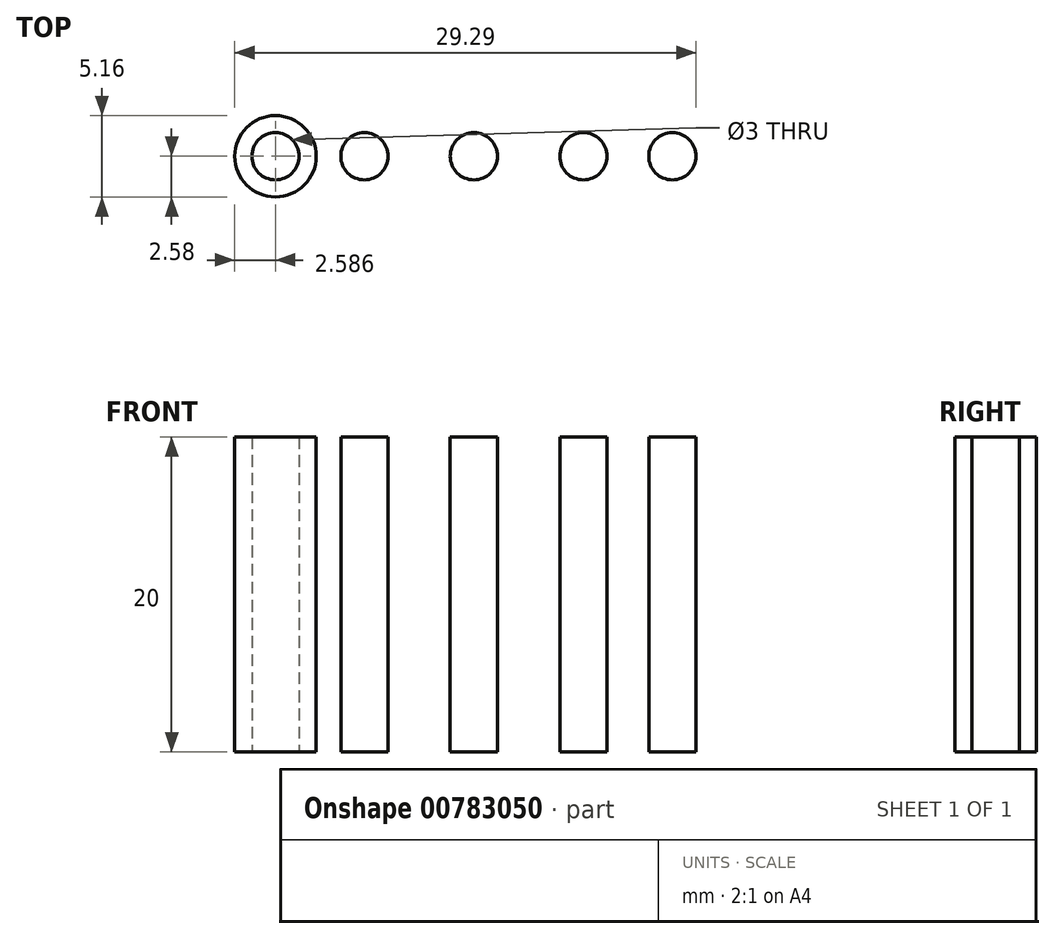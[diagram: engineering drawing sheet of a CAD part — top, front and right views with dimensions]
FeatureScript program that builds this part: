
annotation { "Feature Type Name" : "Feature", "Feature Type Description" : "" }
export const myFeature = defineFeature(function(context is Context, id is Id, definition is map)
    precondition{}
    {
        {
            var Q0;
            Q0=qCreatedBy(makeId("Top.planeOp"),FACE);
            var sketch = newSketch(context, id + "F0", { "sketchPlane" : qUnion([Q0])});
            skCircle(sketch, "E0", {"center": v(0, 0) * mm, "radius": 1.5 * mm});
            skCircle(sketch, "E1", {"center": v(6.95, 0) * mm, "radius": 1.5 * mm});
            skCircle(sketch, "E2", {"center": v(12.6, 0) * mm, "radius": 1.5 * mm});
            skCircle(sketch, "E3.MirrorC", {"center": v(-6.95, 0) * mm, "radius": 1.5 * mm});
            skCircle(sketch, "E4.MirrorC", {"center": v(-12.6, 0) * mm, "radius": 1.5 * mm});
            skCircle(sketch, "E5", {"center": v(-12.6, 0) * mm, "radius": 2.58 * mm});
            skSolve(sketch);
        }
        {
            var Q0;
            Q0 = qSketchRegion(id + "F0", true);
            extrude(context, id + "F1", {"entities" : qUnion([Q0]), "depth" : 20 * mm, "offsetDistance" : 25 * mm});
        }
    });
